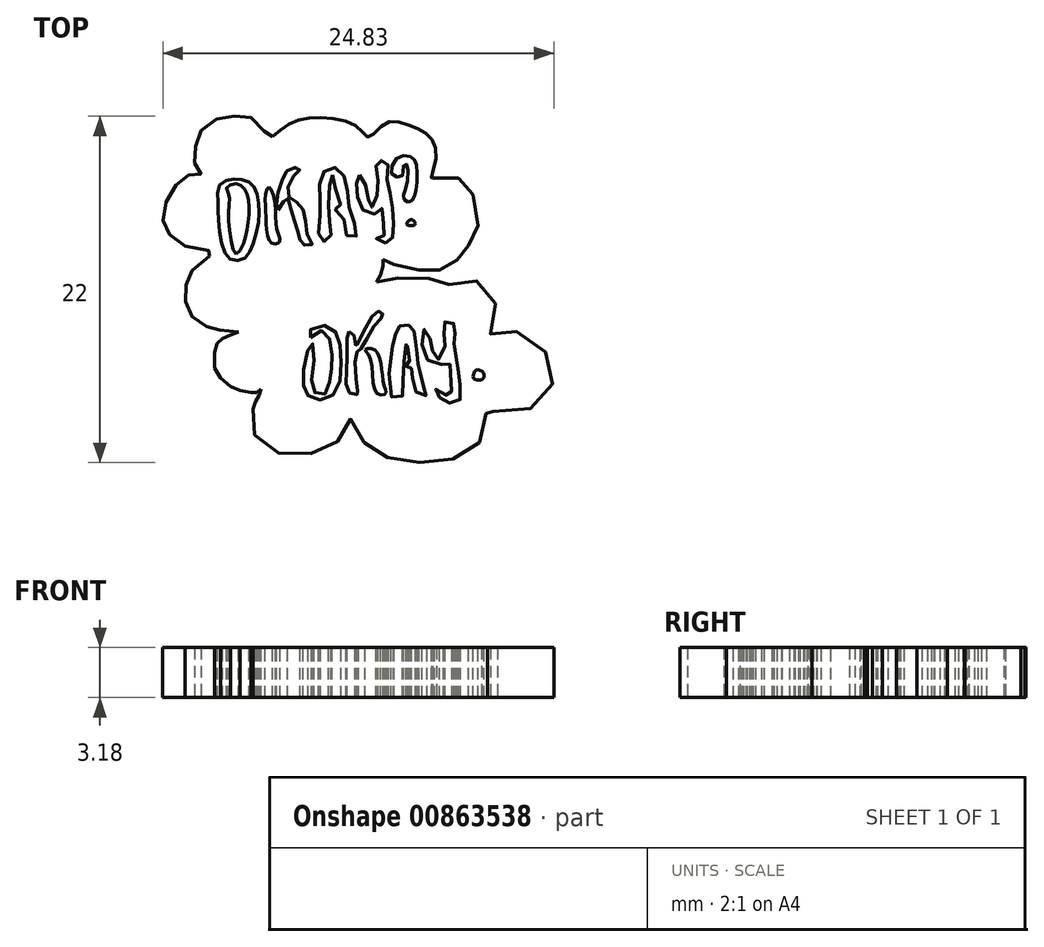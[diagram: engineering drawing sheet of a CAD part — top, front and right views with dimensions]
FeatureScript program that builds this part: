
annotation { "Feature Type Name" : "Feature", "Feature Type Description" : "" }
export const myFeature = defineFeature(function(context is Context, id is Id, definition is map)
    precondition{}
    {
        {
            var Q0;
            Q0=qCreatedBy(makeId("Top.planeOp"),FACE);
            var sketch = newSketch(context, id + "F0", { "sketchPlane" : qUnion([Q0])});
            skFitSpline(sketch, "E0", {"points": [v(31.88, 30.14) * mm, v(33.25, 31.08) * mm, v(35.25, 31.33) * mm, v(37.34, 30.7) * mm, v(37.97, 30.1) * mm, v(39.08, 31) * mm, v(40.49, 30.87) * mm, v(41.72, 30.23) * mm, v(42.28, 28.95) * mm, v(41.98, 27.5) * mm, v(42.02, 27.5) * mm, v(41.98, 27.54) * mm], "startDerivative": vector(11.39, 9.68) * mm, "endDerivative": vector(-3.37, 2.24) * mm});
            skLineSegment(sketch, "E1", {"start": v(42.02, 27.5) * mm, "end": v(43.68, 27.5) * mm});
            skLineSegment(sketch, "E2", {"start": v(43.68, 27.5) * mm, "end": v(44.62, 26.44) * mm});
            skLineSegment(sketch, "E3", {"start": v(44.62, 26.44) * mm, "end": v(44.92, 24.48) * mm});
            skLineSegment(sketch, "E4", {"start": v(44.92, 24.48) * mm, "end": v(44.32, 23.2) * mm});
            skLineSegment(sketch, "E5", {"start": v(44.32, 23.2) * mm, "end": v(43.6, 22.3) * mm});
            skLineSegment(sketch, "E6", {"start": v(43.6, 22.3) * mm, "end": v(42.5, 21.66) * mm});
            skLineSegment(sketch, "E7", {"start": v(42.5, 21.66) * mm, "end": v(41.17, 21.66) * mm});
            skLineSegment(sketch, "E8", {"start": v(41.17, 21.66) * mm, "end": v(39.6, 22) * mm});
            skLineSegment(sketch, "E9", {"start": v(39.6, 22) * mm, "end": v(38.89, 22.32) * mm});
            skLineSegment(sketch, "E10", {"start": v(38.89, 22.32) * mm, "end": v(38.89, 21.9) * mm});
            skLineSegment(sketch, "E11", {"start": v(38.89, 21.9) * mm, "end": v(38.75, 21.32) * mm});
            skLineSegment(sketch, "E12", {"start": v(38.75, 21.32) * mm, "end": v(38.5, 20.9) * mm});
            skLineSegment(sketch, "E13", {"start": v(29.72, 17.72) * mm, "end": v(29.2, 17.53) * mm});
            skLineSegment(sketch, "E14", {"start": v(29.2, 17.53) * mm, "end": v(28.72, 17.3) * mm});
            skLineSegment(sketch, "E15", {"start": v(28.72, 17.3) * mm, "end": v(28.35, 16.98) * mm});
            skLineSegment(sketch, "E16", {"start": v(28.35, 16.98) * mm, "end": v(28.2, 16.4) * mm});
            skLineSegment(sketch, "E17", {"start": v(28.2, 16.4) * mm, "end": v(28.2, 15.89) * mm});
            skLineSegment(sketch, "E18", {"start": v(28.2, 15.89) * mm, "end": v(28.2, 15.42) * mm});
            skLineSegment(sketch, "E19", {"start": v(28.2, 15.42) * mm, "end": v(28.56, 14.79) * mm});
            skLineSegment(sketch, "E20", {"start": v(28.56, 14.79) * mm, "end": v(29.2, 14.25) * mm});
            skLineSegment(sketch, "E21", {"start": v(29.2, 14.25) * mm, "end": v(29.82, 13.99) * mm});
            skLineSegment(sketch, "E22", {"start": v(29.82, 13.99) * mm, "end": v(30.5, 13.89) * mm});
            skLineSegment(sketch, "E23", {"start": v(30.5, 13.89) * mm, "end": v(30.88, 13.89) * mm});
            skLineSegment(sketch, "E24", {"start": v(30.88, 13.89) * mm, "end": v(31.13, 14.1) * mm});
            skLineSegment(sketch, "E25", {"start": v(31.13, 14.1) * mm, "end": v(31, 13.68) * mm});
            skPoint(sketch, "E25.endSnap0", {"position": v(31, 14) * mm});
            skLineSegment(sketch, "E26", {"start": v(31, 13.68) * mm, "end": v(30.8, 13.3) * mm});
            skFitSpline(sketch, "E27", {"points": [v(30.64, 12.84) * mm, v(30.51, 12.27) * mm, v(30.64, 11.4) * mm, v(31.06, 10.76) * mm, v(31.96, 10.12) * mm, v(32.98, 9.93) * mm, v(34.14, 9.96) * mm, v(35.07, 10.24) * mm, v(35.83, 10.64) * mm, v(36.47, 11.21) * mm, v(36.8, 11.9) * mm, v(36.86, 12.24) * mm, v(37.26, 11.45) * mm, v(37.8, 10.56) * mm, v(38.4, 10.05) * mm, v(39.2, 9.73) * mm, v(40.1, 9.52) * mm, v(41.43, 9.43) * mm, v(42.45, 9.47) * mm, v(43.76, 9.8) * mm, v(44.52, 10.28) * mm, v(45.32, 11.1) * mm, v(45.51, 12.2) * mm, v(45.33, 12.77) * mm, v(45.14, 13.24) * mm, v(46, 12.6) * mm, v(47.61, 12.52) * mm, v(48.84, 13.32) * mm, v(49.54, 14.1) * mm, v(49.73, 15.23) * mm, v(49.29, 16.33) * mm, v(48.25, 17.4) * mm, v(47.2, 17.77) * mm, v(46.38, 17.76) * mm, v(45.73, 17.57) * mm, v(46.08, 18.28) * mm, v(46.06, 19.48) * mm, v(45.68, 20.27) * mm, v(44.86, 20.95) * mm, v(43.62, 21.13) * mm, v(43.13, 20.84) * mm, v(42.72, 20.18) * mm, v(41.91, 21.03) * mm, v(40.87, 21.35) * mm, v(39.87, 21.16) * mm, v(39.15, 20.56) * mm, v(38.5, 20.92) * mm, v(38.5, 20.9) * mm], "startDerivative": vector(-10.04, -31.22) * mm, "endDerivative": vector(-1.08, -10.04) * mm});
            skFitSpline(sketch, "E28", {"points": [v(29.72, 17.72) * mm, v(28.45, 17.86) * mm, v(27.9, 17.98) * mm, v(26.98, 18.48) * mm, v(26.42, 19.24) * mm, v(26.34, 20.34) * mm, v(26.5, 21.1) * mm, v(27.17, 22.06) * mm, v(28.2, 22.8) * mm, v(26.97, 22.95) * mm, v(25.54, 23.72) * mm, v(25, 24.44) * mm, v(24.95, 25.46) * mm, v(25.55, 26.77) * mm, v(26.27, 27.52) * mm, v(26.95, 27.8) * mm, v(27.34, 27.76) * mm, v(27, 28.22) * mm, v(26.97, 29.15) * mm, v(27.07, 30.03) * mm, v(27.95, 31.05) * mm, v(29.02, 31.4) * mm, v(30.14, 31.38) * mm, v(30.96, 31.08) * mm, v(31.67, 30.03) * mm, v(31.88, 30.14) * mm], "startDerivative": vector(-30.91, 2.94) * mm, "endDerivative": vector(9.9, 10.94) * mm});
            skFitSpline(sketch, "E29", {"points": [v(29.58, 22.67) * mm, v(30.06, 23.37) * mm, v(30.27, 24.36) * mm, v(30.4, 25.53) * mm, v(30.27, 26.43) * mm, v(29.97, 26.95) * mm, v(29.5, 27.14) * mm, v(28.96, 26.87) * mm, v(29.1, 26.44) * mm, v(29.09, 25.46) * mm, v(29.18, 23.93) * mm, v(29.58, 22.67) * mm]});
            skFitSpline(sketch, "E30", {"points": [v(30.12, 22.43) * mm, v(30.57, 23.15) * mm, v(31, 24.73) * mm, v(30.96, 26.07) * mm, v(30.7, 26.93) * mm, v(30.09, 27.36) * mm, v(29.21, 27.41) * mm, v(28.5, 27) * mm, v(28.4, 26) * mm, v(28.44, 24.84) * mm, v(28.76, 23) * mm, v(29.32, 22.28) * mm, v(30.12, 22.43) * mm]});
            skFitSpline(sketch, "E31", {"points": [v(31.65, 26.92) * mm, v(32.06, 25.76) * mm, v(32.13, 24.32) * mm, v(32.32, 23.45) * mm, v(31.88, 23.32) * mm, v(31.55, 23.87) * mm, v(31.46, 25.23) * mm, v(31.43, 26.34) * mm, v(31.65, 26.92) * mm]});
            skFitSpline(sketch, "E32", {"points": [v(32.22, 25.45) * mm, v(32.77, 26.26) * mm, v(33.06, 25.43) * mm, v(33.45, 24.25) * mm, v(33.68, 23.44) * mm, v(34.06, 23.2) * mm, v(34.46, 23.32) * mm, v(34.24, 23.52) * mm, v(33.97, 24.84) * mm, v(33.5, 25.9) * mm, v(32.87, 26.4) * mm, v(33.24, 27.66) * mm, v(33.61, 28.05) * mm, v(33.04, 28.14) * mm, v(32.46, 27.32) * mm, v(32.12, 25.9) * mm, v(32.22, 25.45) * mm]});
            skFitSpline(sketch, "E33", {"points": [v(35.68, 27.7) * mm, v(35.46, 26.48) * mm, v(35.54, 24.5) * mm, v(35.49, 23.63) * mm, v(34.92, 23.54) * mm, v(34.9, 25.2) * mm, v(34.87, 26.74) * mm, v(35.18, 27.96) * mm, v(36.02, 28.1) * mm, v(36.6, 26.88) * mm, v(36.84, 25.2) * mm, v(37.21, 23.83) * mm, v(36.6, 23.82) * mm, v(36.25, 25.3) * mm, v(35.66, 25.45) * mm, v(36.2, 25.63) * mm, v(36.07, 26.02) * mm, v(35.68, 27.7) * mm]});
            skFitSpline(sketch, "E34", {"points": [v(37.42, 27.7) * mm, v(37.79, 27.07) * mm, v(38.01, 25.9) * mm, v(38.16, 25.63) * mm, v(38.5, 26.33) * mm, v(38.55, 27.5) * mm, v(38.48, 28.48) * mm, v(38.81, 28.62) * mm, v(39.16, 28.48) * mm, v(39.16, 27.45) * mm, v(39.37, 26.41) * mm, v(39.52, 25.11) * mm, v(39.55, 23.92) * mm, v(39.29, 23.4) * mm, v(38.65, 23.5) * mm, v(38.48, 23.68) * mm, v(38.92, 23.81) * mm, v(38.95, 24.34) * mm, v(38.81, 25.58) * mm, v(38.4, 25.23) * mm, v(37.63, 25.45) * mm, v(37.26, 26.43) * mm, v(37.23, 27.4) * mm, v(37.42, 27.7) * mm]});
            skPoint(sketch, "E35.1.internal.orphan", {"position": v(37.42, 28.4) * mm});
            skFitSpline(sketch, "E36", {"points": [v(40.5, 25.97) * mm, v(40.8, 26.16) * mm, v(41.02, 26.86) * mm, v(41.03, 28.3) * mm, v(40.75, 28.79) * mm, v(39.83, 28.8) * mm, v(39.5, 27.7) * mm, v(40.13, 27.65) * mm, v(40.14, 28.1) * mm, v(40.35, 28.4) * mm, v(40.4, 27.03) * mm, v(40.17, 26.28) * mm, v(40.5, 25.97) * mm]});
            skFitSpline(sketch, "E37", {"points": [v(40.5, 25.98) * mm, v(40.84, 25.67) * mm], "startDerivative": vector(0.35, -0.3) * mm, "endDerivative": vector(0.35, -0.3) * mm});
            skFitSpline(sketch, "E38", {"points": [v(40.84, 24.78) * mm, v(40.92, 24.55) * mm, v(40.4, 24.55) * mm, v(40.61, 24.83) * mm, v(40.84, 24.78) * mm]});
            skFitSpline(sketch, "E39", {"points": [v(34.28, 17.38) * mm, v(35.12, 17.82) * mm, v(35.62, 16.7) * mm, v(35.63, 15.55) * mm, v(35.48, 14.41) * mm, v(35.09, 13.7) * mm, v(34.44, 14) * mm, v(34.5, 15.63) * mm, v(34.37, 17.01) * mm, v(33.91, 15.76) * mm, v(33.86, 14.24) * mm, v(34.2, 13.62) * mm, v(35.25, 13.45) * mm, v(36.1, 14.3) * mm, v(36.2, 16.26) * mm, v(35.96, 17.58) * mm, v(35.2, 18.14) * mm, v(34.15, 17.7) * mm, v(34.28, 17.38) * mm]});
            skFitSpline(sketch, "E40", {"points": [v(36.75, 17.75) * mm, v(36.6, 17) * mm, v(36.6, 15.7) * mm, v(36.72, 13.87) * mm, v(37.3, 13.77) * mm, v(37.27, 14.04) * mm, v(37.2, 16.39) * mm, v(37.43, 16.58) * mm, v(38.42, 18.2) * mm, v(38.89, 18.8) * mm, v(38.75, 18.99) * mm, v(38.36, 18.9) * mm, v(37.15, 16.77) * mm, v(37.13, 17.27) * mm, v(36.75, 17.75) * mm]});
            skFitSpline(sketch, "E41", {"points": [v(37.76, 16.6) * mm, v(38.08, 16.05) * mm, v(38.5, 13.82) * mm, v(39.07, 13.82) * mm, v(38.97, 14.28) * mm, v(38.75, 15.77) * mm, v(38.25, 16.65) * mm, v(37.76, 16.6) * mm]});
            skFitSpline(sketch, "E42", {"points": [v(39.5, 16.81) * mm, v(39.45, 13.57) * mm, v(40.08, 13.6) * mm, v(40.16, 14.83) * mm, v(40.32, 16.62) * mm, v(40.4, 17.1) * mm, v(40.52, 16.4) * mm, v(40.55, 15.72) * mm, v(40.37, 15.6) * mm, v(40.37, 15.53) * mm, v(40.66, 15.48) * mm, v(40.68, 15.23) * mm, v(40.84, 14.56) * mm, v(41.16, 13.72) * mm, v(41.67, 13.72) * mm, v(41.5, 14.22) * mm, v(41.22, 15.25) * mm, v(41.12, 15.57) * mm, v(41.1, 15.98) * mm, v(41, 16.73) * mm, v(40.91, 17.36) * mm, v(40.82, 17.86) * mm, v(40.6, 18.12) * mm, v(40.17, 18.17) * mm, v(39.86, 18.02) * mm, v(39.68, 17.53) * mm, v(39.5, 16.81) * mm]});
            skFitSpline(sketch, "E43", {"points": [v(41.9, 17.31) * mm, v(41.98, 16.77) * mm, v(42.08, 16.33) * mm, v(42.34, 15.92) * mm, v(42.66, 16.38) * mm, v(42.83, 16.92) * mm, v(42.8, 17.31) * mm, v(42.74, 17.95) * mm, v(42.77, 18.31) * mm, v(42.98, 18.4) * mm, v(43.24, 18.37) * mm, v(43.45, 18.14) * mm, v(43.47, 17.8) * mm, v(43.46, 17.51) * mm, v(43.44, 17.2) * mm, v(43.4, 16.85) * mm, v(43.49, 16.4) * mm, v(43.62, 15.66) * mm, v(43.67, 15.38) * mm, v(43.77, 14.68) * mm, v(43.78, 13.91) * mm, v(43.76, 13.36) * mm, v(43.4, 13.2) * mm, v(42.95, 13.23) * mm, v(42.63, 13.43) * mm, v(42.28, 13.76) * mm, v(42.17, 14) * mm, v(42.4, 14.11) * mm, v(42.71, 13.9) * mm, v(43.22, 13.5) * mm, v(43.2, 14.52) * mm, v(43.04, 15.96) * mm, v(42.57, 15.64) * mm, v(41.91, 15.8) * mm, v(41.51, 16.23) * mm, v(41.38, 17.24) * mm, v(41.5, 17.85) * mm, v(41.6, 17.95) * mm, v(41.9, 17.31) * mm]});
            skFitSpline(sketch, "E44", {"points": [v(44.98, 15.3) * mm, v(45.23, 15.18) * mm, v(45.3, 14.86) * mm, v(45.13, 14.68) * mm, v(44.7, 14.7) * mm, v(44.63, 14.97) * mm, v(44.79, 15.3) * mm, v(44.98, 15.3) * mm]});
            skLineSegment(sketch, "E45", {"start": v(1.62, 41.75) * mm, "end": v(75.84, 41.75) * mm});
            skLineSegment(sketch, "E46", {"start": v(75.84, 41.75) * mm, "end": v(75.84, 0) * mm});
            skLineSegment(sketch, "E47", {"start": v(75.84, 0) * mm, "end": v(1.62, 0) * mm});
            skLineSegment(sketch, "E48", {"start": v(1.62, 0) * mm, "end": v(1.62, 41.75) * mm});
            skPoint(sketch, "E49.end.orphan", {"position": v(30.64, 12.94) * mm});
            skLineSegment(sketch, "E50", {"start": v(30.8, 13.3) * mm, "end": v(30.64, 12.84) * mm});
            skSolve(sketch);
        }
        {
            var Q0;
            Q0=sQuery(id+"F0.wireOp",EDGE,"E33");
            var Q1;
            Q1=sQuery(id+"F0.wireOp",EDGE,"E30");
            var Q2;
            Q2=sQuery(id+"F0.wireOp",EDGE,"E29");
            var Q3;
            Q3=sQuery(id+"F0.wireOp",EDGE,"E31");
            var Q4;
            Q4=sQuery(id+"F0.wireOp",EDGE,"E32");
            var Q5;
            Q5=sQuery(id+"F0.wireOp",EDGE,"E34");
            var Q6;
            Q6=sQuery(id+"F0.wireOp",EDGE,"E36");
            var Q7;
            Q7=sQuery(id+"F0.wireOp",EDGE,"E38");
            var Q8;
            Q8=sQuery(id+"F0.wireOp",EDGE,"E44");
            var Q9;
            Q9=sQuery(id+"F0.wireOp",EDGE,"E27");
            var Q10;
            Q10=sQuery(id+"F0.wireOp",EDGE,"E28");
            var Q11;
            Q11=sQuery(id+"F0.wireOp",EDGE,"E0");
            extrude(context, id + "F1", {"bodyType" : ToolBodyType.SURFACE, "surfaceEntities" : qUnion([Q0, Q1, Q2, Q3, Q4, Q5, Q6, Q7, Q8, Q9, Q10, Q11]), "depth" : 3.17 * mm, "offsetDistance" : 25.4 * mm});
        }
        {
            var Q0;
            Q0=sQuery(id+"F0.wireOp",EDGE,"E39");
            var Q1;
            Q1=sQuery(id+"F0.wireOp",EDGE,"E40");
            var Q2;
            Q2=sQuery(id+"F0.wireOp",EDGE,"E41");
            var Q3;
            Q3=sQuery(id+"F0.wireOp",EDGE,"E42");
            var Q4;
            Q4=sQuery(id+"F0.wireOp",EDGE,"E43");
            extrude(context, id + "F2", {"bodyType" : ToolBodyType.SURFACE, "surfaceEntities" : qUnion([Q0, Q1, Q2, Q3, Q4]), "depth" : 3.17 * mm, "offsetDistance" : 25.4 * mm});
        }
        {
            var Q0;
            Q0=sQuery(id+"F0.wireOp",EDGE,"E23");
            var Q1;
            Q1=sQuery(id+"F0.wireOp",EDGE,"E24");
            var Q2;
            Q2=sQuery(id+"F0.wireOp",EDGE,"E25");
            var Q3;
            Q3=sQuery(id+"F0.wireOp",EDGE,"E26");
            var Q4;
            Q4=sQuery(id+"F0.wireOp",EDGE,"E50");
            var Q5;
            Q5=sQuery(id+"F0.wireOp",EDGE,"E22");
            var Q6;
            Q6=sQuery(id+"F0.wireOp",EDGE,"E21");
            var Q7;
            Q7=sQuery(id+"F0.wireOp",EDGE,"E20");
            var Q8;
            Q8=sQuery(id+"F0.wireOp",EDGE,"E19");
            var Q9;
            Q9=sQuery(id+"F0.wireOp",EDGE,"E18");
            var Q10;
            Q10=sQuery(id+"F0.wireOp",EDGE,"E17");
            var Q11;
            Q11=sQuery(id+"F0.wireOp",EDGE,"E16");
            var Q12;
            Q12=sQuery(id+"F0.wireOp",EDGE,"E15");
            var Q13;
            Q13=sQuery(id+"F0.wireOp",EDGE,"E14");
            var Q14;
            Q14=sQuery(id+"F0.wireOp",EDGE,"E13");
            extrude(context, id + "F3", {"bodyType" : ToolBodyType.SURFACE, "surfaceEntities" : qUnion([Q0, Q1, Q2, Q3, Q4, Q5, Q6, Q7, Q8, Q9, Q10, Q11, Q12, Q13, Q14]), "depth" : 3.17 * mm, "offsetDistance" : 25.4 * mm});
        }
        {
            var Q0;
            Q0=sQuery(id+"F0.wireOp",EDGE,"E1");
            var Q1;
            Q1=sQuery(id+"F0.wireOp",EDGE,"E2");
            var Q2;
            Q2=sQuery(id+"F0.wireOp",EDGE,"E3");
            var Q3;
            Q3=sQuery(id+"F0.wireOp",EDGE,"E4");
            var Q4;
            Q4=sQuery(id+"F0.wireOp",EDGE,"E5");
            var Q5;
            Q5=sQuery(id+"F0.wireOp",EDGE,"E6");
            var Q6;
            Q6=sQuery(id+"F0.wireOp",EDGE,"E7");
            var Q7;
            Q7=sQuery(id+"F0.wireOp",EDGE,"E8");
            var Q8;
            Q8=sQuery(id+"F0.wireOp",EDGE,"E9");
            var Q9;
            Q9=sQuery(id+"F0.wireOp",EDGE,"E11");
            var Q10;
            Q10=sQuery(id+"F0.wireOp",EDGE,"E10");
            var Q11;
            Q11=sQuery(id+"F0.wireOp",EDGE,"E12");
            extrude(context, id + "F4", {"bodyType" : ToolBodyType.SURFACE, "surfaceEntities" : qUnion([Q0, Q1, Q2, Q3, Q4, Q5, Q6, Q7, Q8, Q9, Q10, Q11]), "depth" : 3.17 * mm, "offsetDistance" : 25.4 * mm});
        }
    });
